# Revit family: AbmessungenKSH_Schlitzzahl = 2
name_source: partatom
category: Air Terminals
revit_build: Autodesk Revit 2017 (Build: 20190508_0315(x64)
units: mm (PartAtom-declared; Revit-internal decimal feet)

## family parameters
Always vertical = Yes
Cut with Voids When Loaded = No
Part Type = Normal
Room Calculation Point = No
Round Connector Dimension = Use Diameter
Shared = No
Work Plane-Based = No

## types (5) — shared parameters
B = 125 mm  [stored 0.410105 ft]
C = 73 mm  [stored 0.239501 ft]
D = 115 mm  [stored 0.377297 ft]
E = 98 mm  [stored 0.321522 ft]
F = 100 mm  [stored 0.328084 ft]
Product material = RAL 9016

## per-type parameters (varying)
| type | A | A1 | Index |
| Nennlänge_500 | 518 mm  [stored 1.69948 ft] | 259 mm  [stored 0.849738 ft] | 1 |
| Nennlänge_600 | 618 mm  [stored 2.02756 ft] | 309 mm  [stored 1.01378 ft] | 2 |
| Nennlänge_800 | 818 mm  [stored 2.68373 ft] | 409 mm  [stored 1.34186 ft] | 3 |
| Nennlänge_1000 | 1018 mm  [stored 3.3399 ft] | 509 mm  [stored 1.66995 ft] | 4 |
| Nennlänge_1200 | 1218 mm  [stored 3.99606 ft] | 609 mm  [stored 1.99803 ft] | 0 |

note: [stored X ft] marks values corroborated as IEEE doubles in the binary element streams (Revit-internal decimal feet)

## geometry (parser evidence)
native form markers: Sweep x2
no freeform markers — native parametric forms only
